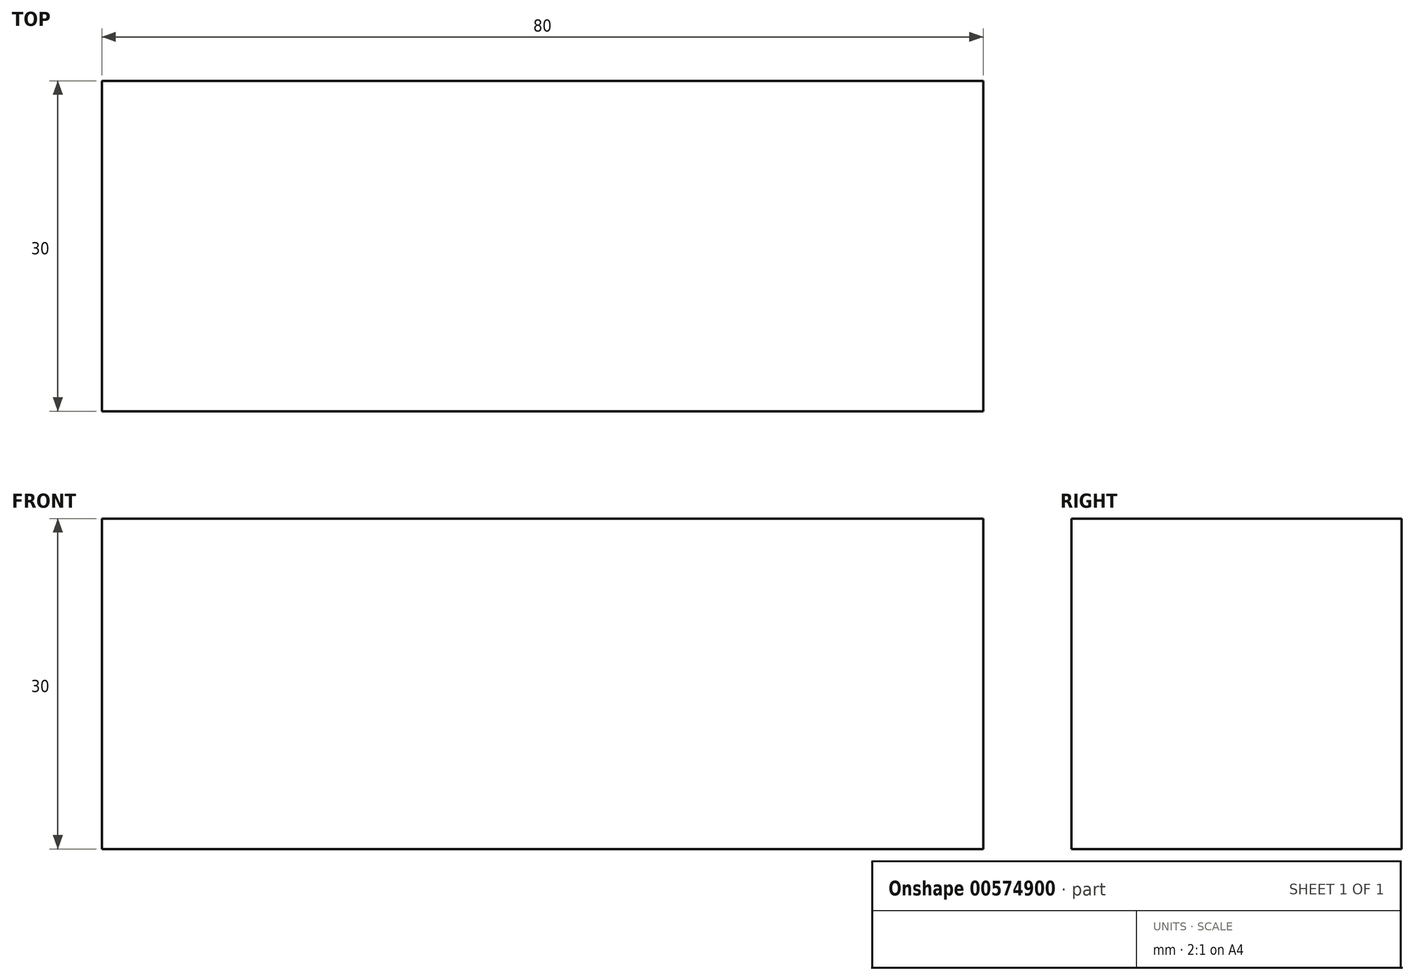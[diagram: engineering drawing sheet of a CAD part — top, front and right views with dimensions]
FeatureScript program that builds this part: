
annotation { "Feature Type Name" : "Feature", "Feature Type Description" : "" }
export const myFeature = defineFeature(function(context is Context, id is Id, definition is map)
    precondition{}
    {
        {
            var Q0;
            Q0=qCreatedBy(makeId("Front.planeOp"),FACE);
            var sketch = newSketch(context, id + "F0", { "sketchPlane" : qUnion([Q0])});
            skLineSegment(sketch, "E0.bottom", {"start": v(-40, 15) * mm, "end": v(40, 15) * mm});
            skLineSegment(sketch, "E0.top", {"start": v(-40, -15) * mm, "end": v(40, -15) * mm});
            skLineSegment(sketch, "E0.left", {"start": v(-40, 15) * mm, "end": v(-40, -15) * mm});
            skLineSegment(sketch, "E0.right", {"start": v(40, 15) * mm, "end": v(40, -15) * mm});
            skPoint(sketch, "E0.middle", {"position": v(0, 0) * mm});
            skSolve(sketch);
        }
        {
            var Q0;
            Q0=makeQuery(id+"F0.imprint","IMPRINT",FACE,{"disambiguationData":[TD([[makeQuery(id+"F0.imprint","IMPRINT",EDGE,{"derivedFrom":sQuery(id+"F0.wireOp",EDGE,"E0.bottom")}),-1.0]])]});
            extrude(context, id + "F1", {"entities" : qUnion([Q0]), "depth" : 30 * mm, "offsetDistance" : 25 * mm});
        }
    });
